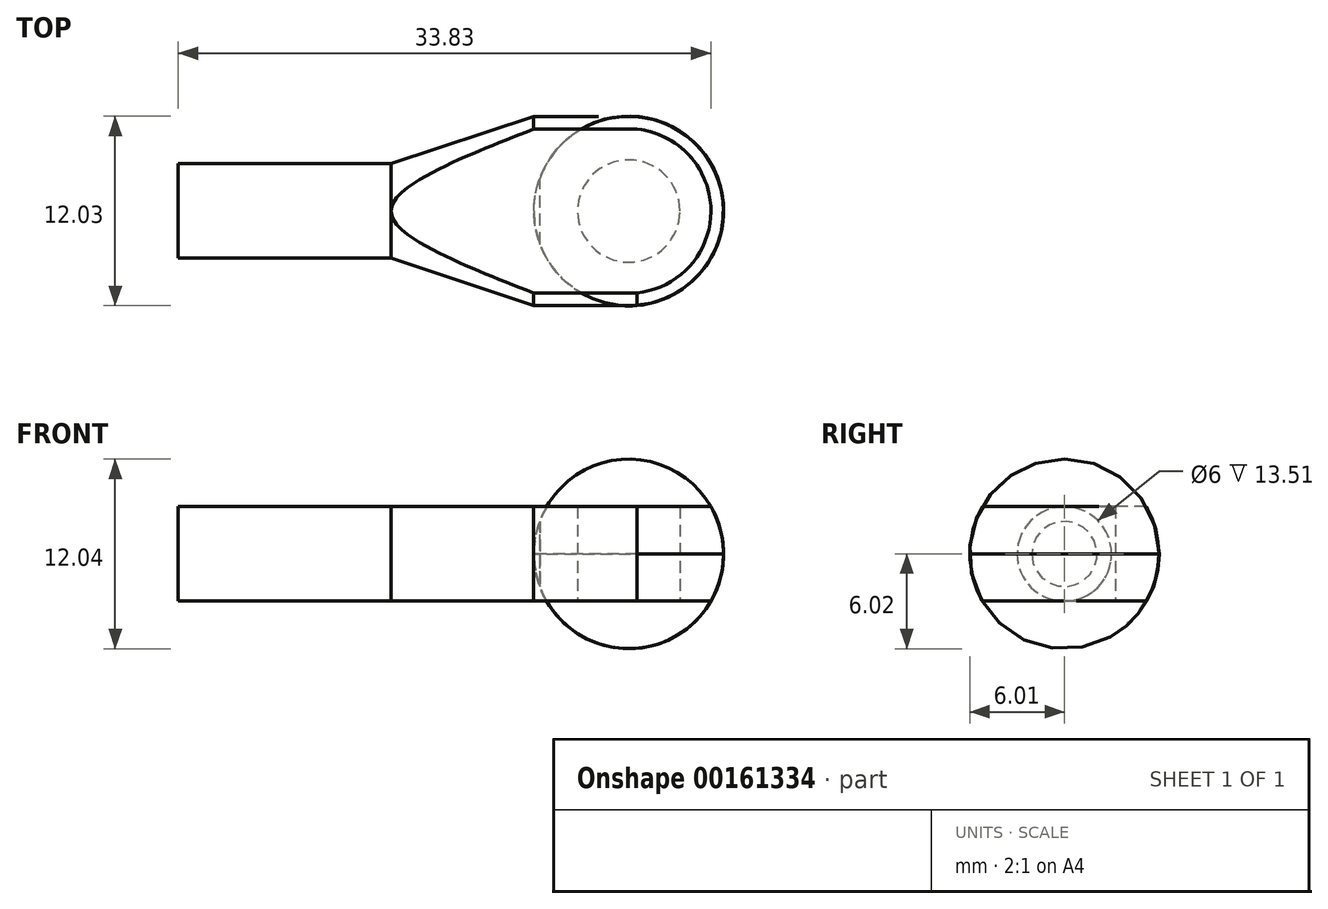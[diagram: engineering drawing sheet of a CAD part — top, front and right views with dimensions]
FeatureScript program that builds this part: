
annotation { "Feature Type Name" : "Feature", "Feature Type Description" : "" }
export const myFeature = defineFeature(function(context is Context, id is Id, definition is map)
    precondition{}
    {
        {
            var Q0;
            Q0=qCreatedBy(makeId("Front.planeOp"),FACE);
            var sketch = newSketch(context, id + "F0", { "sketchPlane" : qUnion([Q0])});
            skLineSegment(sketch, "E0", {"start": v(19.73, 8.5) * mm, "end": v(-14.9, 8.5) * mm});
            skLineSegment(sketch, "E1", {"start": v(-14.9, 8.5) * mm, "end": v(-14.9, 11.5) * mm});
            skLineSegment(sketch, "E2", {"start": v(-14.9, 11.5) * mm, "end": v(-1.39, 11.5) * mm});
            skLineSegment(sketch, "E3", {"start": v(-1.39, 11.5) * mm, "end": v(7.65, 14.5) * mm});
            skLineSegment(sketch, "E4", {"start": v(7.65, 14.5) * mm, "end": v(14.25, 14.5) * mm});
            skArc(sketch, "E5", {"start": v(14.25, 14.5) * mm, "mid": v(18.16, 12.56) * mm, "end": v(19.73, 8.5) * mm});
            skPoint(sketch, "E6.orphan", {"position": v(19.17, 8.5) * mm});
            skSolve(sketch);
        }
        {
            var Q0;
            Q0=makeQuery(id+"F0.imprint","IMPRINT",FACE,{"disambiguationData":[TD([[makeQuery(id+"F0.imprint","IMPRINT",EDGE,{"derivedFrom":sQuery(id+"F0.wireOp",EDGE,"E0")}),-1.0]])]});
            var Q1;
            Q1=sQuery(id+"F0.wireOp",EDGE,"E0");
            revolve(context, id + "F1", {"entities" : qUnion([Q0]), "axis" : qUnion([Q1]), "revolveType" : RevolveType.SYMMETRIC, "angle" : 180 * degree});
        }
        {
            var Q0;
            Q0=qCreatedBy(makeId("Top.planeOp"),FACE);
            cPlane(context, id + "F2", {"entities" : qUnion([Q0]), "cplaneType" : CPlaneType.OFFSET, "offset" : 25 * mm, "width" : 150 * mm, "height" : 150 * mm});
        }
        {
            var Q0;
            Q0=qCreatedBy(id+"F2.planeOp",FACE);
            var sketch = newSketch(context, id + "F3", { "sketchPlane" : qUnion([Q0])});
            skLineSegment(sketch, "E7.bottom", {"start": v(42.89, 44.14) * mm, "end": v(-167.24, 44.14) * mm});
            skLineSegment(sketch, "E7.top", {"start": v(42.89, -51.02) * mm, "end": v(-167.24, -51.02) * mm});
            skLineSegment(sketch, "E7.left", {"start": v(42.89, 44.14) * mm, "end": v(42.89, -51.02) * mm});
            skLineSegment(sketch, "E7.right", {"start": v(-167.24, 44.14) * mm, "end": v(-167.24, -51.02) * mm});
            skSolve(sketch);
        }
        {
            var Q0;
            Q0=makeQuery(id+"F3.imprint","IMPRINT",FACE,{"disambiguationData":[TD([[makeQuery(id+"F3.imprint","IMPRINT",EDGE,{"derivedFrom":sQuery(id+"F3.wireOp",EDGE,"E7.bottom")}),1.0]])]});
            extrude(context, id + "F4", {"entities" : qUnion([Q0]), "operationType" : NewBodyOperationType.REMOVE, "oppositeDirection" : true, "depth" : 13.5 * mm});
        }
        {
            var Q0;
            Q0=makeQuery(id+"F1.opRevolve","CAP_FACE",FACE,{"disambiguationData":[OSD([sQuery(id+"F0.wireOp",EDGE,"E0"),sQuery(id+"F0.wireOp",EDGE,"E1"),sQuery(id+"F0.wireOp",EDGE,"E2"),sQuery(id+"F0.wireOp",EDGE,"E3"),sQuery(id+"F0.wireOp",EDGE,"E4"),sQuery(id+"F0.wireOp",EDGE,"E5")])],"isStart":false});
            var sketch = newSketch(context, id + "F5", { "sketchPlane" : qUnion([Q0])});
            skCircle(sketch, "E8", {"center": v(13.71, 0) * mm, "radius": 3.25 * mm});
            skSolve(sketch);
        }
        {
            var Q0;
            Q0=makeQuery(id+"F5.imprint","IMPRINT",FACE,{"disambiguationData":[TD([[makeQuery(id+"F5.imprint","IMPRINT",EDGE,{"derivedFrom":sQuery(id+"F5.wireOp",EDGE,"E8")}),1.0]])]});
            extrude(context, id + "F6", {"entities" : qUnion([Q0]), "operationType" : NewBodyOperationType.REMOVE, "endBound" : BoundingType.THROUGH_ALL, "oppositeDirection" : true, "depth" : 25 * mm});
        }
        {
            var Q0;
            Q0=makeQuery(id+"F1.opRevolve","SWEPT_BODY",BODY,{"disambiguationData":[OSD([sQuery(id+"F0.wireOp",EDGE,"E0"),sQuery(id+"F0.wireOp",EDGE,"E1"),sQuery(id+"F0.wireOp",EDGE,"E2"),sQuery(id+"F0.wireOp",EDGE,"E3"),sQuery(id+"F0.wireOp",EDGE,"E4"),sQuery(id+"F0.wireOp",EDGE,"E5")])]});
            var Q1;
            Q1=makeQuery(id+"F1.opRevolve","CAP_FACE",FACE,{"disambiguationData":[OSD([sQuery(id+"F0.wireOp",EDGE,"E0"),sQuery(id+"F0.wireOp",EDGE,"E1"),sQuery(id+"F0.wireOp",EDGE,"E2"),sQuery(id+"F0.wireOp",EDGE,"E3"),sQuery(id+"F0.wireOp",EDGE,"E4"),sQuery(id+"F0.wireOp",EDGE,"E5")])],"isStart":false});
            mirror(context, id + "F7", {"operationType" : NewBodyOperationType.ADD, "entities" : qUnion([Q0]), "mirrorPlane" : qUnion([Q1])});
        }
    });
